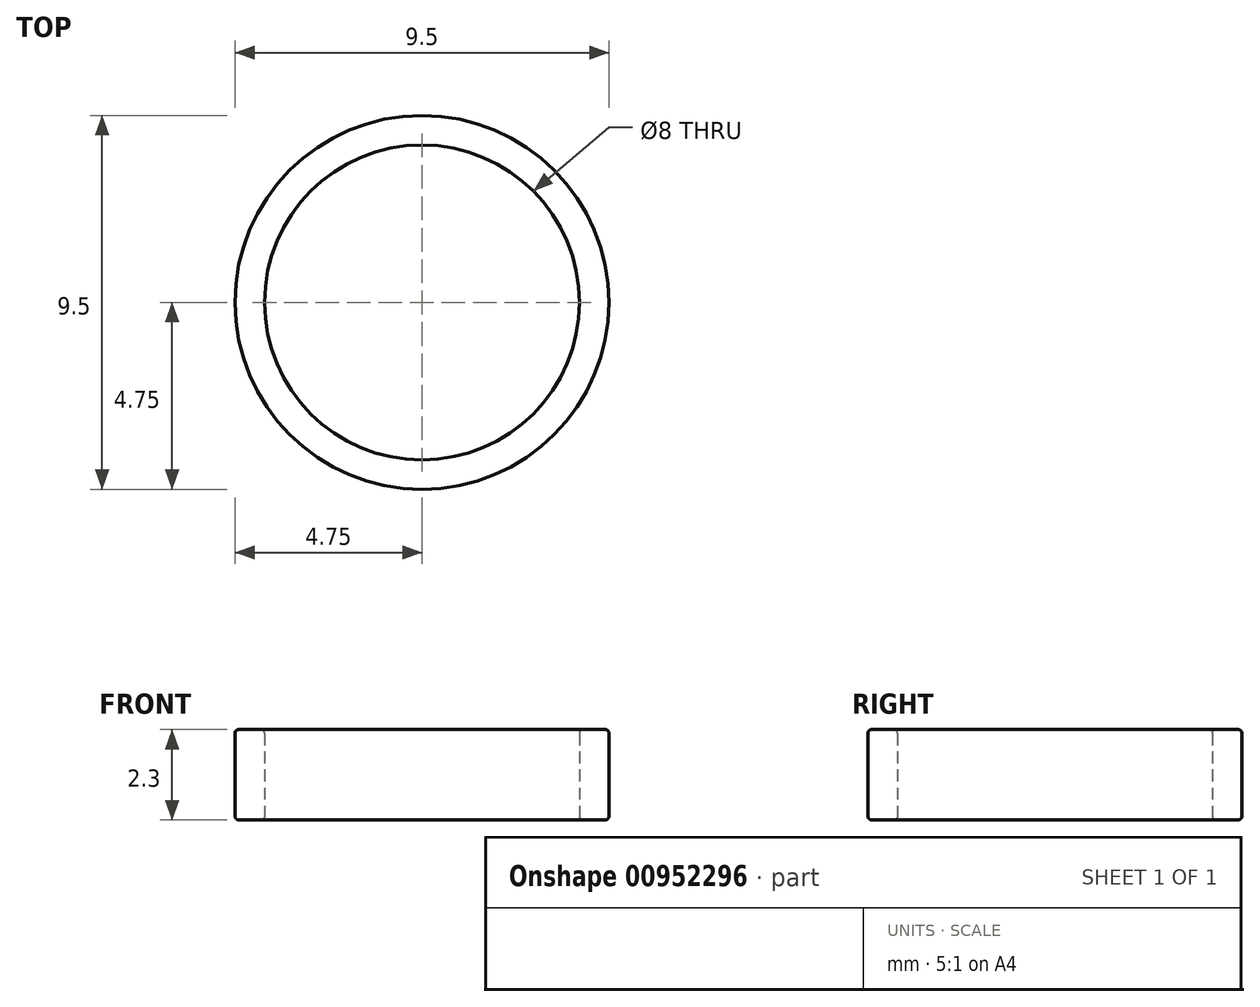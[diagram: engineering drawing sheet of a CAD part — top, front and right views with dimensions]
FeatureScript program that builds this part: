
annotation { "Feature Type Name" : "Feature", "Feature Type Description" : "" }
export const myFeature = defineFeature(function(context is Context, id is Id, definition is map)
    precondition{}
    {
        {
            var Q0;
            Q0=qCreatedBy(makeId("Top.planeOp"),FACE);
            var sketch = newSketch(context, id + "F0", { "sketchPlane" : qUnion([Q0])});
            skCircle(sketch, "E0", {"center": v(0, 0) * mm, "radius": 4.75 * mm});
            skCircle(sketch, "E1", {"center": v(0, 0) * mm, "radius": 4 * mm});
            skSolve(sketch);
        }
        {
            var Q0;
            Q0=qSketchRegion(id+"F0",true);
            var Q1;
            Q1 = qConstructionFilter(qBodyType(qCreatedBy(id + "F0" ,EDGE), BodyType.WIRE), ConstructionObject.NO);
            extrude(context, id + "F1", {"entities" : qUnion([Q0]), "surfaceEntities" : qUnion([Q1]), "depth" : 2.3 * mm, "offsetDistance" : 25 * mm});
        }
        {
            var Q0;
            Q0=makeQuery(id+"F1.opExtrude","CAP_FACE",FACE,{"disambiguationData":[OSD([sQuery(id+"F0.wireOp",EDGE,"E0"),sQuery(id+"F0.wireOp",EDGE,"E1")])],"isStart":false});
            var Q1;
            Q1=makeQuery(id+"F1.opExtrude","CAP_FACE",FACE,{"disambiguationData":[OSD([sQuery(id+"F0.wireOp",EDGE,"E0"),sQuery(id+"F0.wireOp",EDGE,"E1")])],"isStart":true});
            fillet(context, id + "F2", {"entities" : qUnion([Q0, Q1]), "radius" : 0.1 * mm, "tangentPropagation" : true, "allowEdgeOverflow" : false});
        }
    });
